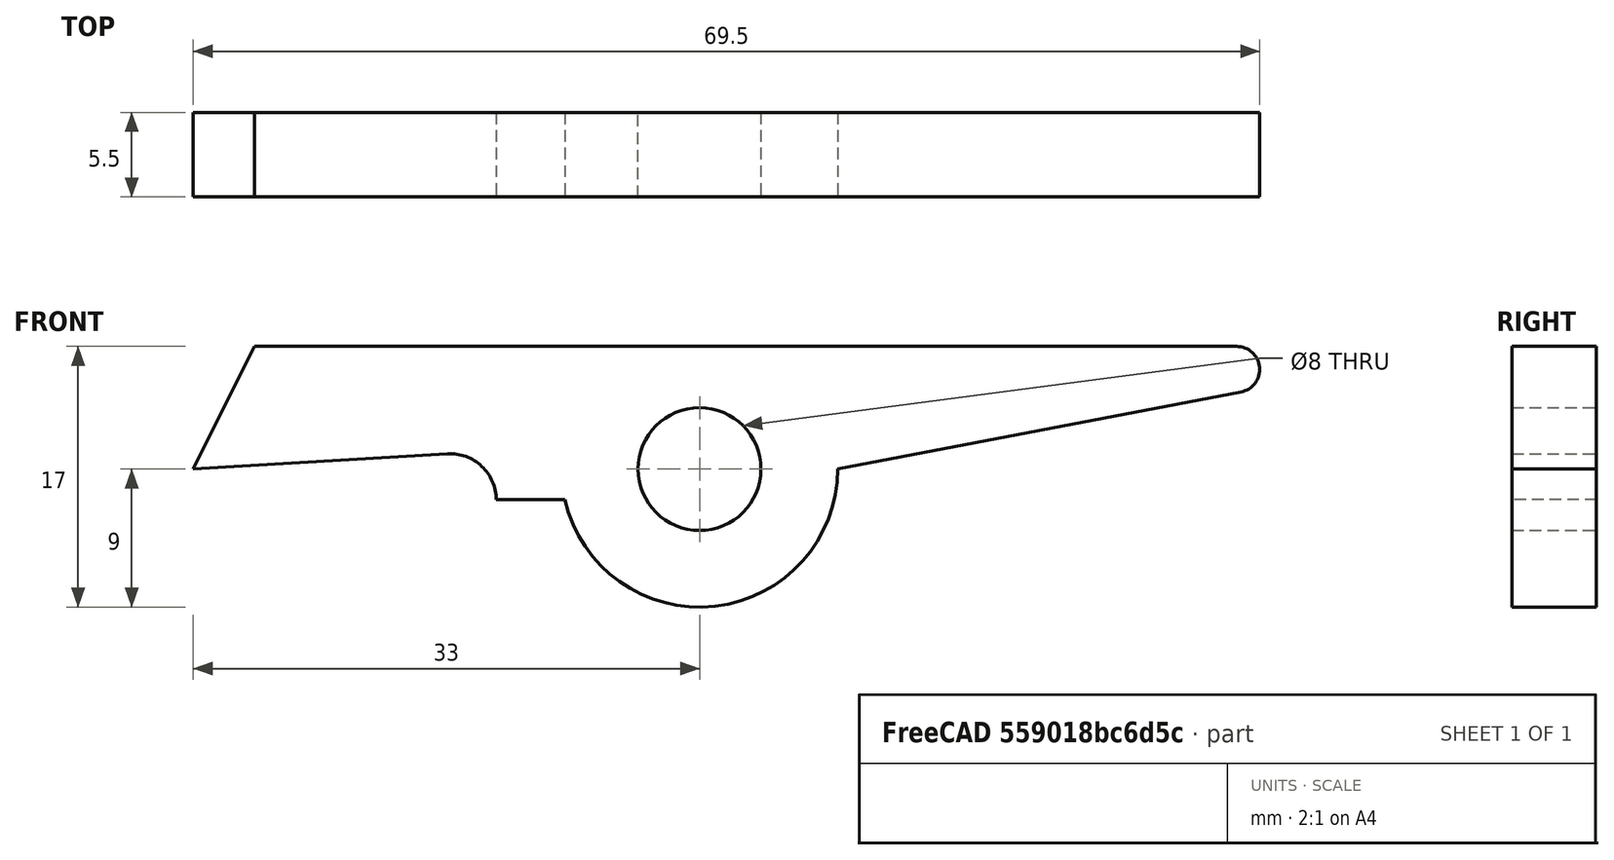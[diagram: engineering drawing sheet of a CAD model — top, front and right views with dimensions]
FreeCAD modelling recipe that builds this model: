
FCSTD DOCUMENT  (FreeCAD 0.16RUnknown)
Label: bloqueo
License: All rights reserved
LicenseURL: http://en.wikipedia.org/wiki/All_rights_reserved
objects: Sketcher::SketchObject×1, PartDesign::Pad×1
note: 3 computed .brp shape members not serialized (recipe doc carries the construction recipe); baked Part::Feature solids carry a one-line shape summary decoded from their .brp

FEATURE [Sketcher::SketchObject] Sketch
  Placement = pos=(0,0,0) rot=(-1,0,0;4.71239rad)
  sketch-geometry (9):
    g0: LineSegment StartX=-29 StartY=8 StartZ=0 EndX=35 EndY=8 EndZ=0
    g1: LineSegment StartX=-29 StartY=8 StartZ=0 EndX=-33 EndY=0 EndZ=0
    g2: LineSegment StartX=-33 StartY=0 StartZ=0 EndX=-16.4295 EndY=0.99461 EndZ=0
    g3: ArcOfCircle CenterX=35 CenterY=6.5 CenterZ=0 NormalX=0 NormalY=0 NormalZ=1 Radius=1.5 StartAngle=4.90137 EndAngle=7.85398
    g4: Circle CenterX=0 CenterY=0 CenterZ=0 NormalX=0 NormalY=0 NormalZ=1 Radius=4
    g5: ArcOfCircle CenterX=0 CenterY=0 CenterZ=0 NormalX=0 NormalY=0 NormalZ=1 Radius=9 StartAngle=3.36569 EndAngle=6.28319
    g6: LineSegment StartX=9 StartY=0 StartZ=0 EndX=35.2818 EndY=5.02671 EndZ=0
    g7: LineSegment StartX=-8.77496 StartY=-2 StartZ=0 EndX=-13.2498 EndY=-2 EndZ=0
    g8: ArcOfCircle CenterX=-16.2498 CenterY=-2 CenterZ=0 NormalX=0 NormalY=0 NormalZ=1 Radius=3 StartAngle=0 EndAngle=1.63075
  constraints (28):
    c: Horizontal(g0)
    c: Coincident(g1,g0)
    c: PointOnObject(g1,g-1)
    c: Coincident(g2,g1)
    c: DistanceX(g0,g-1) = 29
    c: DistanceX(g-1,g0) = 35
    c: Coincident(g3,g0)
    c: Tangent(g3,g0)
    c: Radius(g3) = 1.5
    c: DistanceY(g-1,g0) = 8
    c: Coincident(g4,g-1)
    c: Radius(g4) = 4
    c: Coincident(g5,g-1)
    c: Radius(g5) = 9
    c: Coincident(g6,g5)
    c: Coincident(g6,g3)
    c: Tangent(g3,g6)
    c: PointOnObject(g5,g-1)
    c: DistanceY(g5,g0) = 10
    c: Coincident(g7,g5)
    c: Horizontal(g7)
    c: DistanceX(g1,g0) = 4
    c: Angle(g2,g1) = 1.0472
    c: Coincident(g8,g7)
    c: Radius(g8) = 3
    c: Coincident(g8,g2)
    c: Tangent(g2,g8)
    c: Perpendicular(g8,g7)
FEATURE [PartDesign::Pad] Pad
  Length = 5.5
  Length2 = 100
  Placement = pos=(0,0,0) rot=(-1,0,0;4.71239rad)
  Sketch = -> Sketch
  Type = 0
